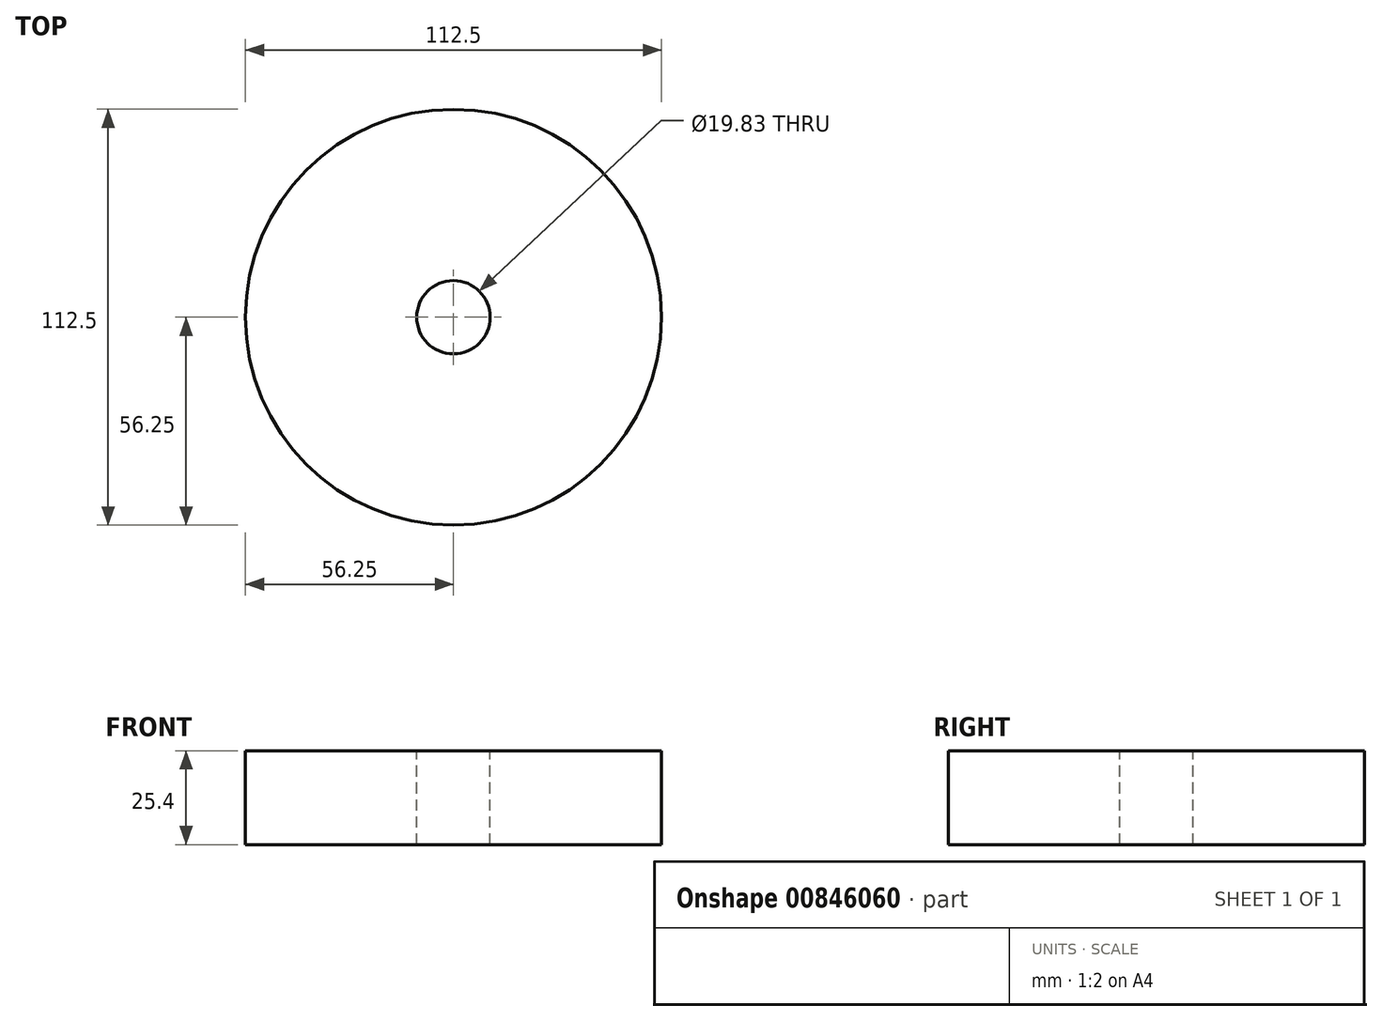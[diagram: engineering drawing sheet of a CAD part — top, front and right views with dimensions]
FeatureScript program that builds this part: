
annotation { "Feature Type Name" : "Feature", "Feature Type Description" : "" }
export const myFeature = defineFeature(function(context is Context, id is Id, definition is map)
    precondition{}
    {
        {
            var Q0;
            Q0=qCreatedBy(makeId("Top.planeOp"),FACE);
            var sketch = newSketch(context, id + "F0", { "sketchPlane" : qUnion([Q0])});
            skCircle(sketch, "E0", {"center": v(0, 0) * mm, "radius": 56.25 * mm});
            skSolve(sketch);
        }
        {
            var Q0;
            Q0=qSketchRegion(id+"F0",true);
            extrude(context, id + "F1", {"entities" : qUnion([Q0]), "depth" : 25.4 * mm, "offsetDistance" : 25.4 * mm});
        }
        {
            var Q0;
            Q0=qCreatedBy(makeId("Top.planeOp"),FACE);
            var sketch = newSketch(context, id + "F2", { "sketchPlane" : qUnion([Q0])});
            skCircle(sketch, "E1", {"center": v(0, 0) * mm, "radius": 9.92 * mm});
            skSolve(sketch);
        }
        {
            var Q0;
            Q0=qSketchRegion(id+"F2",true);
            extrude(context, id + "F3", {"entities" : qUnion([Q0]), "operationType" : NewBodyOperationType.REMOVE, "endBound" : BoundingType.THROUGH_ALL, "oppositeDirection" : true, "depth" : 25.4 * mm, "offsetDistance" : 25.4 * mm, "hasSecondDirection" : true, "secondDirectionOppositeDirection" : false, "secondDirectionDepth" : 25.4 * mm});
        }
    });
